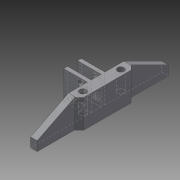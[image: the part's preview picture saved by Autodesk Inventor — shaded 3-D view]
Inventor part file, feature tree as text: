
AUTODESK INVENTOR PART (.ipt)
format: ipt  version: 2015 (Build 190159000, 159)  size: 183,808 bytes
history: native  units: mm
features: sketch x6, extrude x4, chamfer x4, hole x2
ambient origin geometry x8: Origin, YZ Plane, XZ Plane, XY Plane, X Axis, Y Axis, Z Axis, Center Point
bodies: Solid1 (feature_tree)
feature tree (16):
  extrude  "Extrusion1"  Depth=4.0mm
  hole  "Hole1"  [1 undecoded]
  hole  "Hole2"  [1 undecoded]
  chamfer  "Chamfer1"  Distance=10.0mm
  extrude  "Extrusion2"  TaperAngle=0.0deg  [1 undecoded]
  extrude  "Extrusion3"  Depth=7.0mm
  extrude  "Extrusion4"  Depth=5.0mm TaperAngle=45.0deg
  chamfer  "Chamfer2"  Distance=60.0mm
  chamfer  "Chamfer3"  Distance=60.0mm
  chamfer  "Chamfer4"  Distance=30.0mm
  sketch  "Sketch1"  dims[d0=10.5mm d1=4.0mm]
  sketch  "Sketch2"  dims[d2=4.0mm d3=12.0mm]
  sketch  "Sketch3"  dims[d4=25.0mm d5=30.0mm d6=0.0mm]
  sketch  "Sketch4"  dims[d7=5.0mm]
  sketch  "Sketch5"  dims[d8=5.0mm]
  sketch  "Sketch6"  dims[d9=5.0mm d10=10.0mm d11=0.0mm d12=7.0mm d13=3.0mm d14=6.0mm d15=6.0mm d16=2.0mm d17=90.0deg d18=8.0mm d19=20.594885mm d20=3.0mm d21=6.0mm d22=6.0mm d23=2.0mm d24=90.0deg d25=8.0mm d26=20.594885mm d27=5.0mm d28=2.0mm d29=45.0deg d30=60.0mm d31=60.0mm d32=30.0mm d33=0.0mm d34=25.0mm d35=25.0mm d36=30.0mm d37=0.0mm d38=40.0mm d39=6.0mm d40=6.0mm d41=5.0mm d42=7.0mm d43=7.0mm d44=20.0mm d45=0.0mm d46=5.0mm d47=60.0mm d48=45.0deg d49=20.0mm d50=40.0mm d51=45.0deg d52=20.0mm d53=40.0mm d54=45.0deg]
note: 3 required parameter values undecoded (feature->parameter linkage not recoverable at this tier; creation-order binding heuristic only, values carry confidence <= 0.55)
